# Revit family: P100_Pulsador convencional de extinción
name_source: partatom
category: Dispositivos de alarma de incendios
revit_build: Autodesk Revit 2017 (Build: 20190508_0315(x64)
units: mm (PartAtom-declared; Revit-internal decimal feet)

## family parameters
Anfitrión = Cara
Compartido = No
Corte con vacíos al cargar = No
Cota de conector redondo = Diámetro de uso
Mantener orientación de anotación = No
Punto de cálculo de habitación = No
Tipo de pieza = Normal

## types (2) — shared parameters
Altura = 87 mm
Anchura = 87 mm
Carga eléctrica = Otro
Certificación = EN 54-11 y EN 54-17
Comentarios de tipo = Los pulsadores convencionales de Detnov permiten la activación manual inmediata de una alarma en caso de incendio. Es uno de los dispositivos básicos en cualquier sistema de detección y extinción, ya que permite la activación por parte del usuario en caso de localizar un incendio, previamente a la entrada de una alarma del sistema automático de detección.
Conexionado = 2 x 1,5 mm² trenzado
Consumo en alarma = < 100 mA
Consumo en reposo = < 100 μA
Elevación por defecto = 1219 mm
Fabricante = Detnov Security
Fases = 1
Humedad relativa = 95% sin condensación
Imagen de tipo = <Ninguno>
Potencia total = 0 VA
Profundidad = 59 mm
Teléfono = (+34) 93 371 60 25
Temperatura trabajo = De -10ºC a 70ºC
Tensión de trabajo = De 9 a 28VCC
URL = https://www.detnov.com
Voltaje = 230 V
Índice IP = IP40

## per-type parameters (varying)
| type | Cuerpo | Código de montaje | Descripción | Modelo |
| PPD-100 | ABS azul | PDETPPD-100 | Pulsador de paro de extinción rearmable. Marca Detnov, modelo PPD-100. Color azul. Con llave de prueba, montaje en superficie. Uso en interior. Incluye resistencia de 100 Ohm -2W. Dimensiones 98x98x48mm. Certificado CPR EN54-11. | Pulsador PPD-100 |
| PDD-100 | ABS amarillo | PDETPDD-100 | Pulsador de disparo de extinción rearmable. Marca Detnov, modelo PDD-100. Color amarillo. Con llave de prueba, montaje en superficie. Uso en interior. Incluye resistencia de 100 Ohm -2W. Dimensiones 98x98x48mm. Certificado CPR EN54-11. | Pulsador PDD-100 |
